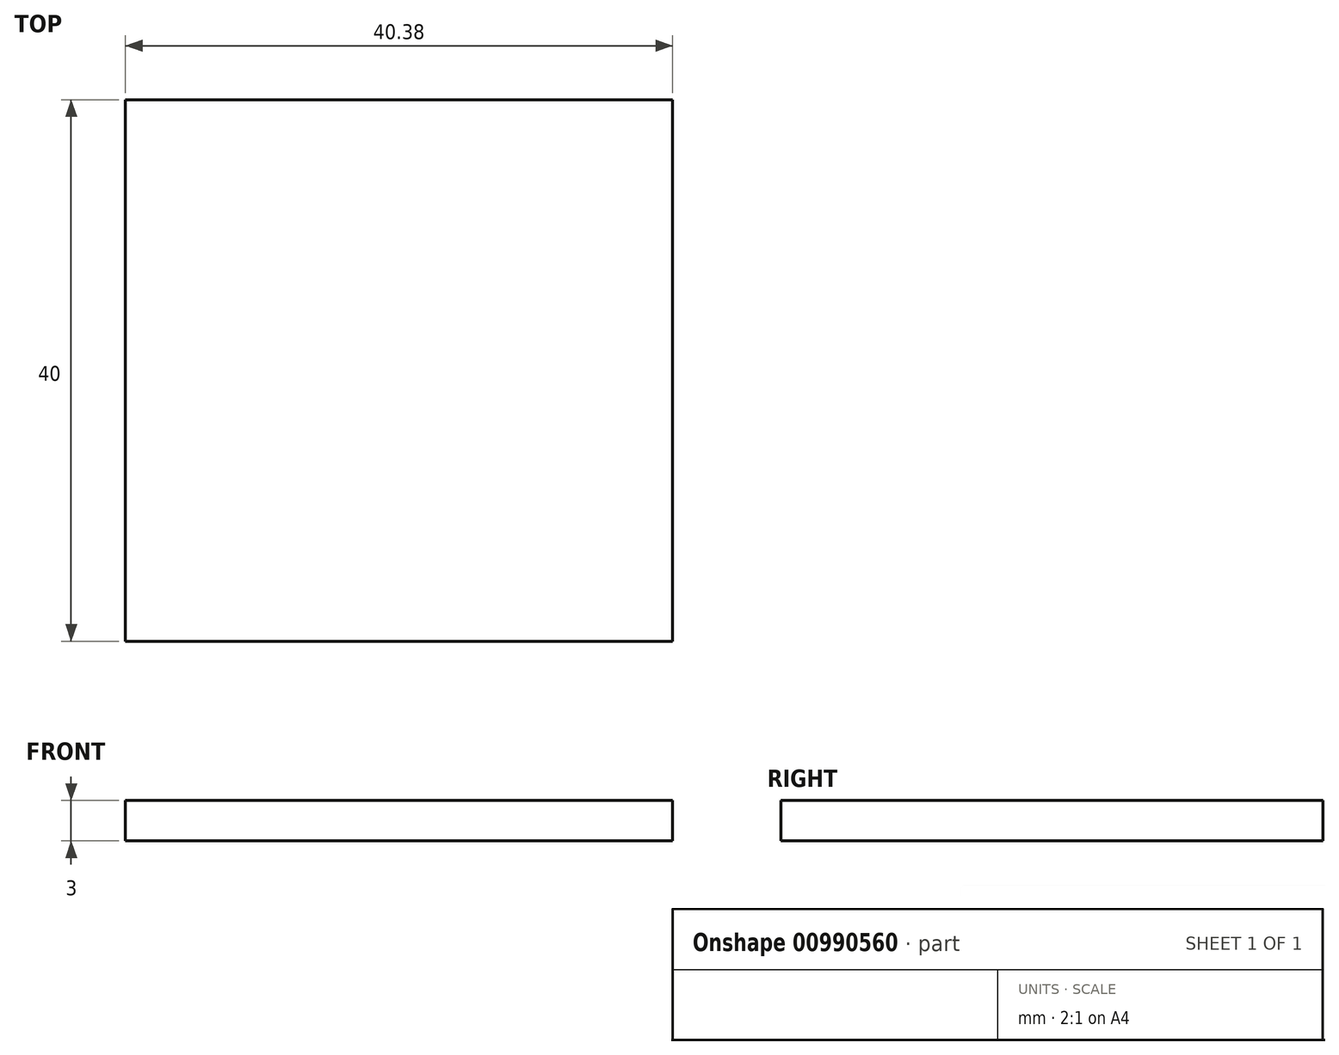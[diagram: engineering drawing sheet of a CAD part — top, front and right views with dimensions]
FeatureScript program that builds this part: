
annotation { "Feature Type Name" : "Feature", "Feature Type Description" : "" }
export const myFeature = defineFeature(function(context is Context, id is Id, definition is map)
    precondition{}
    {
        {
            var Q0;
            Q0=qCreatedBy(makeId("Top.planeOp"),FACE);
            var sketch = newSketch(context, id + "F0", { "sketchPlane" : qUnion([Q0])});
            skLineSegment(sketch, "E0.bottom", {"start": v(0, 0) * mm, "end": v(40.38, 0) * mm});
            skLineSegment(sketch, "E0.top", {"start": v(0, 40) * mm, "end": v(40.38, 40) * mm});
            skLineSegment(sketch, "E0.left", {"start": v(0, 0) * mm, "end": v(0, 40) * mm});
            skLineSegment(sketch, "E0.right", {"start": v(40.38, 0) * mm, "end": v(40.38, 40) * mm});
            skSolve(sketch);
        }
        {
            var Q0;
            Q0=makeQuery(id+"F0.imprint","IMPRINT",FACE,{"disambiguationData":[TD([[makeQuery(id+"F0.imprint","IMPRINT",EDGE,{"derivedFrom":sQuery(id+"F0.wireOp",EDGE,"E0.bottom")}),1.0]])]});
            extrude(context, id + "F1", {"entities" : qUnion([Q0]), "depth" : 3 * mm, "offsetDistance" : 25 * mm});
        }
    });
